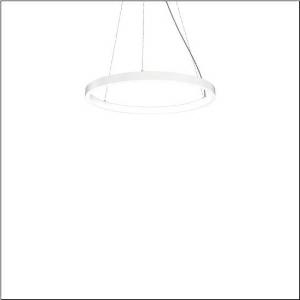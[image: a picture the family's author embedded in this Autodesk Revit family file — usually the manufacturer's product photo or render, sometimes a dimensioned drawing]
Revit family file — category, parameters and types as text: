
# Revit family: silica_r__21_ring-i_5pjbi2d3004a_f975
name_source: partatom
category: Lighting Fixtures
units: mm (PartAtom-declared; Revit-internal decimal feet)

## family parameters
Cut with Voids When Loaded = No
Host = Face
Light Source = No
Part Type = Normal
Room Calculation Point = No
Round Connector Dimension = Use Diameter
Shared = No

## types (1)
- Silica® 21 Ring-I (1 x LED, 5040 lm, 80 W, 4000K)
    Apparent Load = 80 VA
    CIE Flux Codes = 22 48 76 50 101
    Color Rendering = 80
    Color Temperature = 4000K
    Default Elevation = 1800 mm
    Description = Silica® 21 Ring-I, suspended luminaire, of PMMA, frosted, light emission: inner ring side luminous distribution, primary light characteristic: symmetric, installation type: suspended mounting, LED, rated luminous flux: 5.040lm, luminous efficacy: 63lm/W, light colour: 840, colour temperature: 4000K, control gear: DALI 2, with terminal, 5-pole, mains connection: 230V, AC/DC, 0/50..60Hz, rated input power: 80W, housing, of extruded aluminium section, traffic white (RAL 9016), diameter: 805mm, ceiling canopy, traffic white (RAL 9016), protection rating (lamp compartment): IP40, insulation class (complete): insulation class I (protective earthing), certification: CE, impact resistance: IK02, permissible operating ambient temperature: 0..+35°C, packaging unit: 1 piece
    Height = 48 mm  [stored 0.15748 ft]
    Lamp = 1 x LED
    Lamp Light Flux = 5040 lm
    Lamp Power = 80 W
    Lamp count = 1
    Length = 805 mm
    Luminous efficacy = 63 lm/W
    Manufacturer = Siteco
    ModVariant = No
    Model = 5PJBI2D3004A
    Mounting Place = Ceiling
    Mounting Type = Pendant
    Number of Poles = 1
    OnlyDefault = Yes
    Power Factor = 1
    Product Name = Silica® 21 Ring-I
    Product group = suspended luminaire
    ProductGroupID = 905
    Protection Class = Protection class I
    Protection Degree = IP 40
    RLX_Detail_Level = 1
    RLX_Emergency_Light_Flux = 0 lm
    RLX_Emergency_Type = 0
    RLX_Emergency_Type_DB = No
    RlxData = <blob elided: 11585 chars, md5=dbc649c8>
    Socket = socket
    Standby Power = 0 W
    System Light Flux = 5040 lm
    System Power = 80 W
    Type Comments = Product without accessories
    Type Image = l_1258367.jpg
    URL = http://relux.com
    VarID = ---
    Voltage = 0 V
    Weight = 0.00 kg
    Width = 0 mm  [stored 0 ft]

note: [stored X ft] marks values corroborated as IEEE doubles in the binary element streams (Revit-internal decimal feet)

## geometry (parser evidence)
native form markers: Sweep x11
no freeform markers — native parametric forms only
